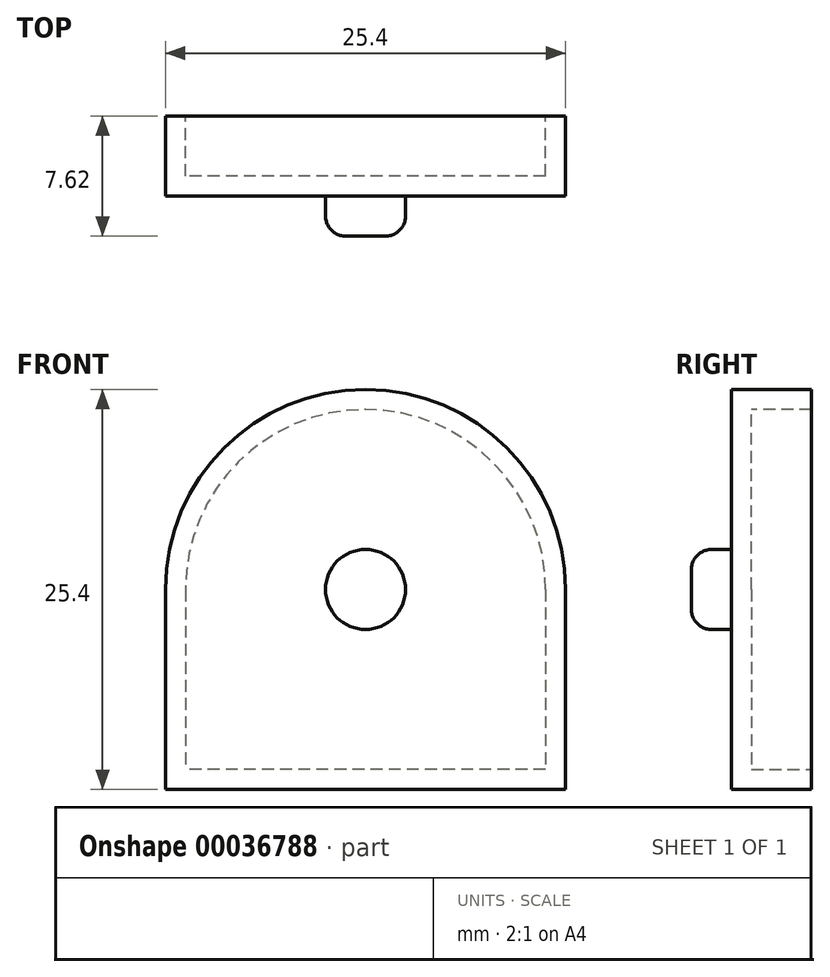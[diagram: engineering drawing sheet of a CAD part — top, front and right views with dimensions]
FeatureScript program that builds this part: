
annotation { "Feature Type Name" : "Feature", "Feature Type Description" : "" }
export const myFeature = defineFeature(function(context is Context, id is Id, definition is map)
    precondition{}
    {
        {
            var Q0;
            Q0=qCreatedBy(makeId("Front.planeOp"),FACE);
            var sketch = newSketch(context, id + "F0", { "sketchPlane" : qUnion([Q0])});
            skLineSegment(sketch, "E0.rect.bottom", {"start": v(12.7, 12.7) * mm, "end": v(-12.7, 12.7) * mm});
            skLineSegment(sketch, "E0.rect.top", {"start": v(12.7, -12.7) * mm, "end": v(-12.7, -12.7) * mm});
            skLineSegment(sketch, "E0.rect.left", {"start": v(12.7, 12.7) * mm, "end": v(12.7, -12.7) * mm});
            skLineSegment(sketch, "E0.rect.right", {"start": v(-12.7, 12.7) * mm, "end": v(-12.7, -12.7) * mm});
            skPoint(sketch, "E0.rect.middle", {"position": v(0, 0) * mm});
            skSolve(sketch);
        }
        {
            var Q0;
            Q0 = qSketchRegion(id + "F0", true);
            extrude(context, id + "F1", {"entities" : qUnion([Q0]), "depth" : 5.08 * mm});
        }
        {
            var Q0;
            Q0=makeQuery(id+"F1.opExtrude","SWEPT_EDGE",EDGE,{"disambiguationData":[OSD([sQuery(id+"F0.wireOp",EDGE,"E0.rect.bottom"),sQuery(id+"F0.wireOp",EDGE,"E0.rect.left")])]});
            var Q1;
            Q1=makeQuery(id+"F1.opExtrude","SWEPT_EDGE",EDGE,{"disambiguationData":[OSD([sQuery(id+"F0.wireOp",EDGE,"E0.rect.bottom"),sQuery(id+"F0.wireOp",EDGE,"E0.rect.right")])]});
            fillet(context, id + "F2", {"entities" : qUnion([Q0, Q1]), "radius" : 12.7 * mm, "tangentPropagation" : true, "allowEdgeOverflow" : false});
        }
        {
            var Q0;
            Q0=makeQuery(id+"F1.opExtrude","CAP_FACE",FACE,{"disambiguationData":[OSD([sQuery(id+"F0.wireOp",EDGE,"E0.rect.bottom"),sQuery(id+"F0.wireOp",EDGE,"E0.rect.top"),sQuery(id+"F0.wireOp",EDGE,"E0.rect.left"),sQuery(id+"F0.wireOp",EDGE,"E0.rect.right")])],"isStart":true});
            shell(context, id + "F3", {"entities" : qUnion([Q0]), "thickness" : 1.27 * mm});
        }
        {
            var Q0;
            Q0=makeQuery(id+"F1.opExtrude","CAP_FACE",FACE,{"disambiguationData":[OSD([sQuery(id+"F0.wireOp",EDGE,"E0.rect.bottom"),sQuery(id+"F0.wireOp",EDGE,"E0.rect.top"),sQuery(id+"F0.wireOp",EDGE,"E0.rect.left"),sQuery(id+"F0.wireOp",EDGE,"E0.rect.right")])],"isStart":false});
            var sketch = newSketch(context, id + "F4", { "sketchPlane" : qUnion([Q0])});
            skCircle(sketch, "E1", {"center": v(0, 0) * mm, "radius": 2.54 * mm});
            skSolve(sketch);
        }
        {
            var Q0;
            Q0=makeQuery(id+"F4.imprint","IMPRINT",FACE,{"disambiguationData":[TD([[makeQuery(id+"F4.imprint","IMPRINT",EDGE,{"derivedFrom":sQuery(id+"F4.wireOp",EDGE,"E1")}),1.0]])]});
            extrude(context, id + "F5", {"entities" : qUnion([Q0]), "operationType" : NewBodyOperationType.ADD, "depth" : 2.54 * mm});
        }
        {
            var Q0;
            Q0=makeQuery(id+"F5.opExtrude","CAP_EDGE",EDGE,{"disambiguationData":[OSD([sQuery(id+"F4.wireOp",EDGE,"E1")])],"isStart":false});
            fillet(context, id + "F6", {"entities" : qUnion([Q0]), "radius" : 1.27 * mm, "tangentPropagation" : true, "allowEdgeOverflow" : false});
        }
    });
